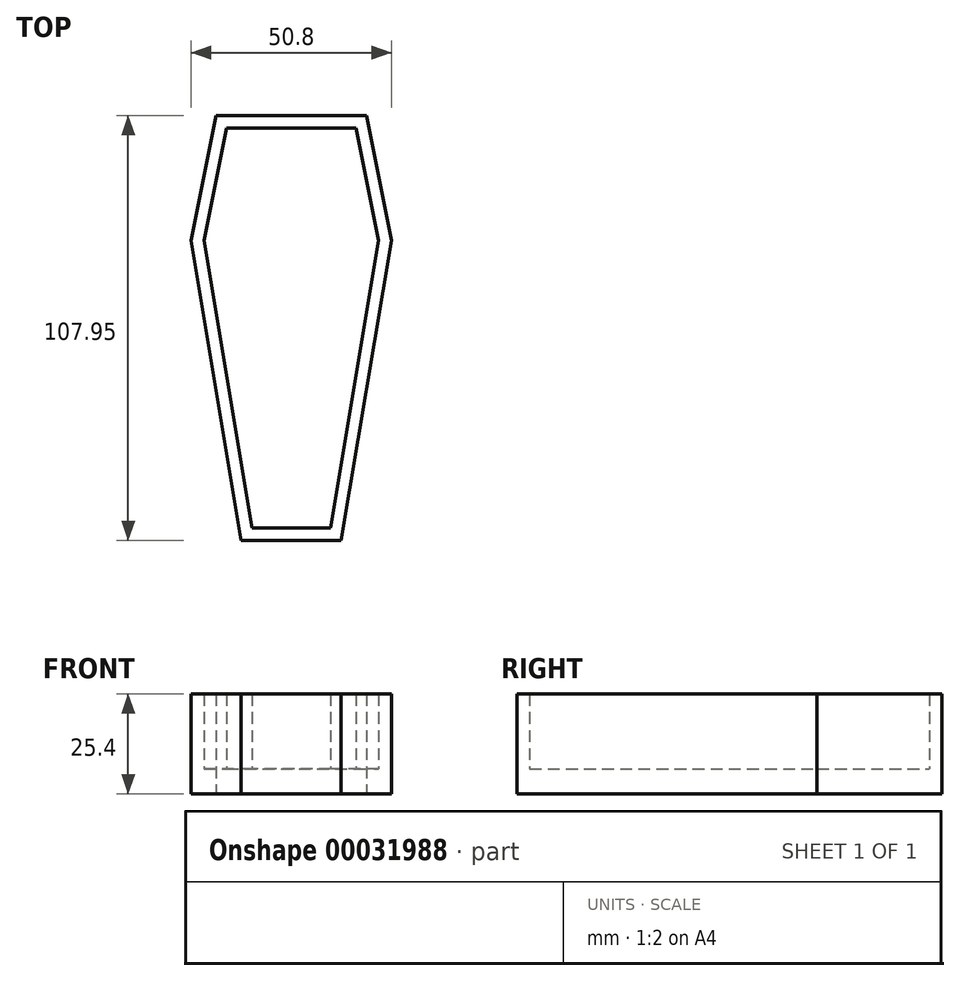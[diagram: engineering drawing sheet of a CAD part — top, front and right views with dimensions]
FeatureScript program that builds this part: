
annotation { "Feature Type Name" : "Feature", "Feature Type Description" : "" }
export const myFeature = defineFeature(function(context is Context, id is Id, definition is map)
    precondition{}
    {
        {
            var Q0;
            Q0=qCreatedBy(makeId("Top.planeOp"),FACE);
            var sketch = newSketch(context, id + "F0", { "sketchPlane" : qUnion([Q0])});
            skLineSegment(sketch, "E0", {"start": v(-19.05, 38.1) * mm, "end": v(19.05, 38.1) * mm});
            skLineSegment(sketch, "E1", {"start": v(19.05, 38.1) * mm, "end": v(25.4, 6.35) * mm});
            skLineSegment(sketch, "E2", {"start": v(25.4, 6.35) * mm, "end": v(12.7, -69.85) * mm});
            skLineSegment(sketch, "E3", {"start": v(12.7, -69.85) * mm, "end": v(-12.7, -69.85) * mm});
            skLineSegment(sketch, "E4", {"start": v(-12.7, -69.85) * mm, "end": v(-25.4, 6.35) * mm});
            skLineSegment(sketch, "E5", {"start": v(-25.4, 6.35) * mm, "end": v(-19.05, 38.1) * mm});
            skLineSegment(sketch, "E6", {"start": v(0, 0) * mm, "end": v(0, 38.1) * mm, "construction": true});
            skSolve(sketch);
        }
        {
            var Q0;
            Q0 = qSketchRegion(id + "F0", true);
            extrude(context, id + "F1", {"entities" : qUnion([Q0]), "depth" : 6.35 * mm});
        }
        {
            var Q0;
            Q0=makeQuery(id+"F1.opExtrude","CAP_FACE",FACE,{"disambiguationData":[OSD([sQuery(id+"F0.wireOp",EDGE,"E0"),sQuery(id+"F0.wireOp",EDGE,"E1"),sQuery(id+"F0.wireOp",EDGE,"E2"),sQuery(id+"F0.wireOp",EDGE,"E3"),sQuery(id+"F0.wireOp",EDGE,"E4"),sQuery(id+"F0.wireOp",EDGE,"E5")])],"isStart":false});
            var sketch = newSketch(context, id + "F2", { "sketchPlane" : qUnion([Q0])});
            skLineSegment(sketch, "E7.0", {"start": v(-25.4, 6.35) * mm, "end": v(-19.05, 38.1) * mm});
            skLineSegment(sketch, "E7.1", {"start": v(-12.7, -69.85) * mm, "end": v(-25.4, 6.35) * mm});
            skLineSegment(sketch, "E7.2", {"start": v(12.7, -69.85) * mm, "end": v(-12.7, -69.85) * mm});
            skLineSegment(sketch, "E7.3", {"start": v(25.4, 6.35) * mm, "end": v(12.7, -69.85) * mm});
            skLineSegment(sketch, "E7.4", {"start": v(19.05, 38.1) * mm, "end": v(25.4, 6.35) * mm});
            skLineSegment(sketch, "E7.5", {"start": v(-19.05, 38.1) * mm, "end": v(19.05, 38.1) * mm});
            skLineSegment(sketch, "E8.0", {"start": v(-22.17, 6.3) * mm, "end": v(-16.45, 34.93) * mm});
            skLineSegment(sketch, "E8.1", {"start": v(-10.01, -66.67) * mm, "end": v(-22.17, 6.3) * mm});
            skLineSegment(sketch, "E8.2", {"start": v(10.01, -66.67) * mm, "end": v(-10.01, -66.67) * mm});
            skLineSegment(sketch, "E8.3", {"start": v(22.17, 6.3) * mm, "end": v(10.01, -66.68) * mm});
            skLineSegment(sketch, "E8.4", {"start": v(16.45, 34.93) * mm, "end": v(22.17, 6.3) * mm});
            skLineSegment(sketch, "E8.5", {"start": v(-16.45, 34.93) * mm, "end": v(16.45, 34.93) * mm});
            skSolve(sketch);
        }
        {
            var Q0;
            Q0 = qSketchRegion(id + "F2", true);
            extrude(context, id + "F3", {"entities" : qUnion([Q0]), "operationType" : NewBodyOperationType.ADD, "depth" : 19.05 * mm});
        }
    });
